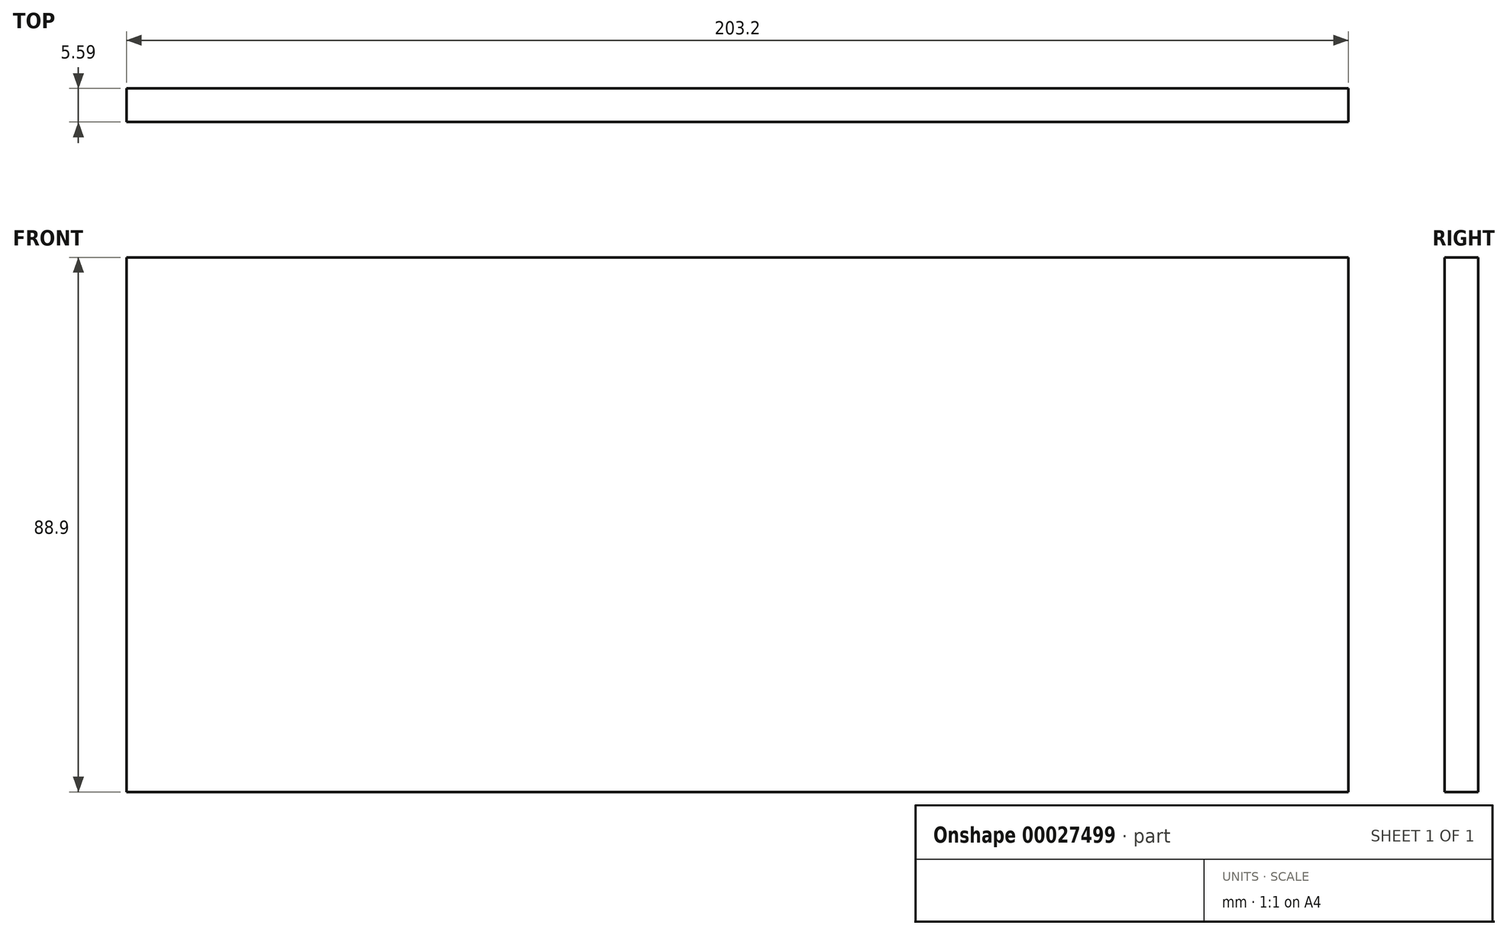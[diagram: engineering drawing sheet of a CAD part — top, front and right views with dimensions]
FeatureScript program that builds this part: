
annotation { "Feature Type Name" : "Feature", "Feature Type Description" : "" }
export const myFeature = defineFeature(function(context is Context, id is Id, definition is map)
    precondition{}
    {
        {
            var Q0;
            Q0=qCreatedBy(makeId("Front.planeOp"),FACE);
            var sketch = newSketch(context, id + "F0", { "sketchPlane" : qUnion([Q0])});
            skLineSegment(sketch, "E0.rect.bottom", {"start": v(101.6, -44.45) * mm, "end": v(-101.6, -44.45) * mm});
            skLineSegment(sketch, "E0.rect.top", {"start": v(101.6, 44.45) * mm, "end": v(-101.6, 44.45) * mm});
            skLineSegment(sketch, "E0.rect.left", {"start": v(101.6, -44.45) * mm, "end": v(101.6, 44.45) * mm});
            skLineSegment(sketch, "E0.rect.right", {"start": v(-101.6, -44.45) * mm, "end": v(-101.6, 44.45) * mm});
            skPoint(sketch, "E0.rect.middle", {"position": v(0, 0) * mm});
            skSolve(sketch);
        }
        {
            var Q0;
            Q0 = qSketchRegion(id + "F0", true);
            extrude(context, id + "F1", {"entities" : qUnion([Q0]), "depth" : 5.6 * mm});
        }
    });
